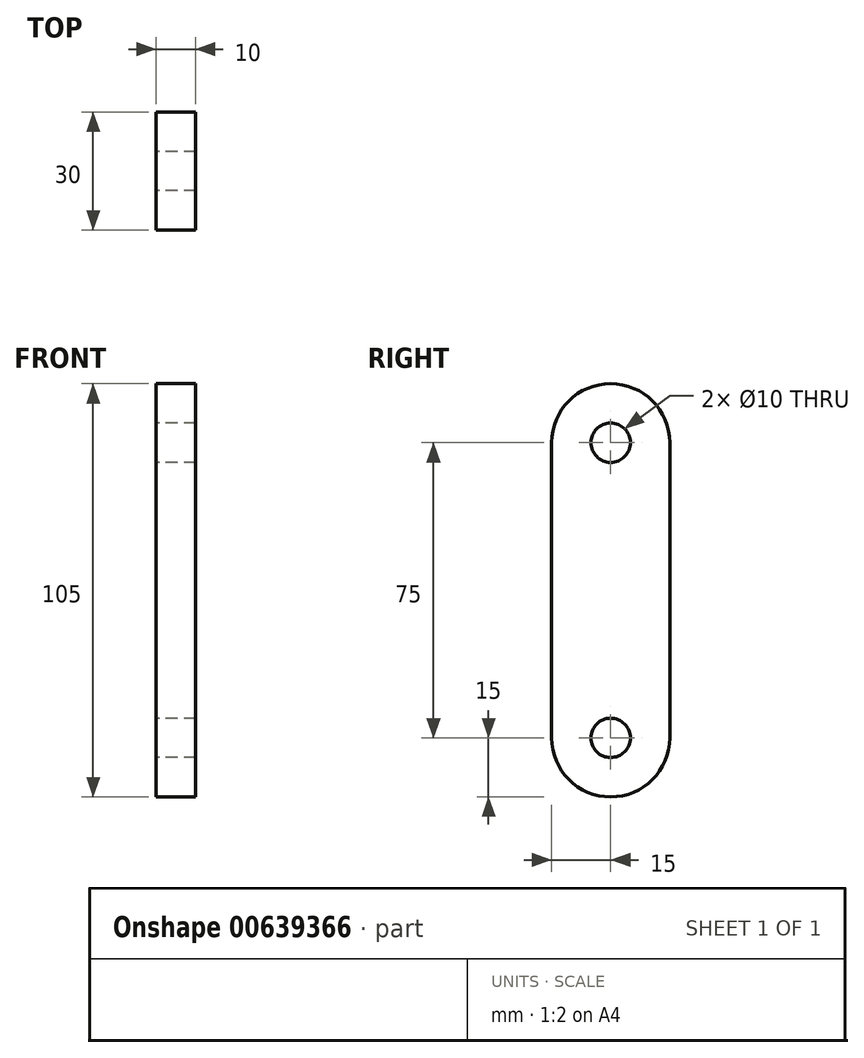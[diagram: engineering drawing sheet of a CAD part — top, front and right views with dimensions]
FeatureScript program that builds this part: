
annotation { "Feature Type Name" : "Feature", "Feature Type Description" : "" }
export const myFeature = defineFeature(function(context is Context, id is Id, definition is map)
    precondition{}
    {
        {
            var Q0;
            Q0=qCreatedBy(makeId("Right.planeOp"),FACE);
            var sketch = newSketch(context, id + "F0", { "sketchPlane" : qUnion([Q0])});
            skCircle(sketch, "E0", {"center": v(0, 0) * mm, "radius": 5 * mm});
            skArc(sketch, "E1", {"start": v(-15, 0) * mm, "mid": v(0, -15) * mm, "end": v(15, 0) * mm});
            skLineSegment(sketch, "E2", {"start": v(0, 0) * mm, "end": v(5, 0) * mm});
            skLineSegment(sketch, "E3", {"start": v(-15, 0) * mm, "end": v(-15, 75) * mm});
            skLineSegment(sketch, "E4", {"start": v(15, 0) * mm, "end": v(15, 75) * mm});
            skCircle(sketch, "E5", {"center": v(0, 75) * mm, "radius": 5 * mm});
            skArc(sketch, "E6", {"start": v(15, 75) * mm, "mid": v(0, 90) * mm, "end": v(-15, 75) * mm});
            skLineSegment(sketch, "E7", {"start": v(0, 0) * mm, "end": v(15, 0) * mm});
            skLineSegment(sketch, "E8", {"start": v(0, 75) * mm, "end": v(15, 75) * mm});
            skLineSegment(sketch, "E9", {"start": v(-15, 75) * mm, "end": v(15, 75) * mm});
            skSolve(sketch);
        }
        {
            var Q0;
            Q0=qSketchRegion(id+"F0",true);
            extrude(context, id + "F1", {"entities" : qUnion([Q0]), "depth" : 10 * mm});
        }
    });
